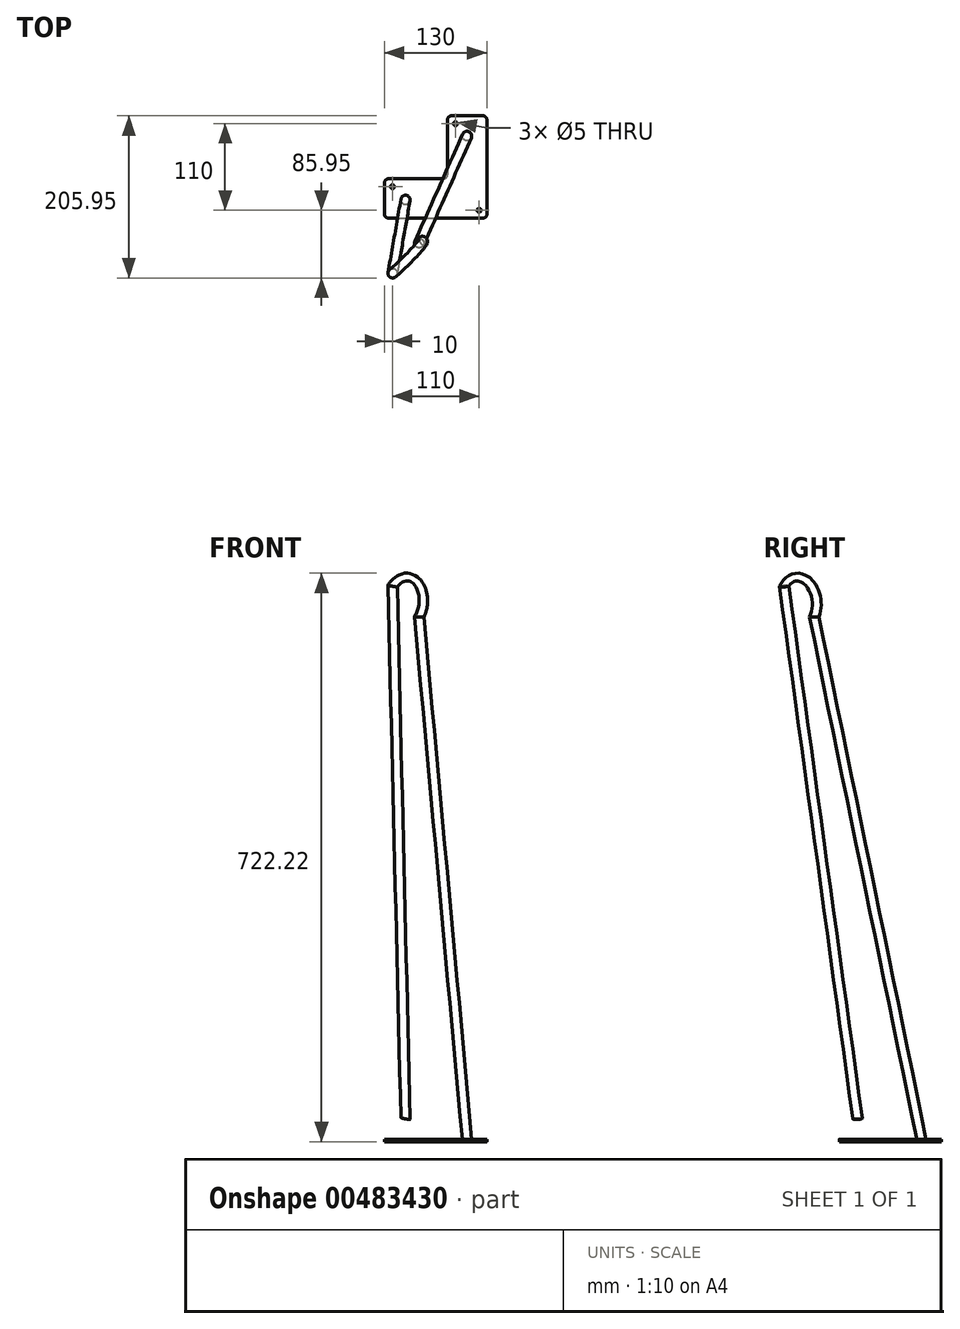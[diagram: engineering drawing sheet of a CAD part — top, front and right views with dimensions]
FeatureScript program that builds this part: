
annotation { "Feature Type Name" : "Feature", "Feature Type Description" : "" }
export const myFeature = defineFeature(function(context is Context, id is Id, definition is map)
    precondition{}
    {
        {
            var Q0;
            Q0=qCreatedBy(makeId("Top.planeOp"),FACE);
            var sketch = newSketch(context, id + "F0", { "sketchPlane" : qUnion([Q0])});
            skLineSegment(sketch, "E0", {"start": v(0, 0) * mm, "end": v(130, 0) * mm});
            skLineSegment(sketch, "E1", {"start": v(130, 0) * mm, "end": v(130, 130) * mm});
            skLineSegment(sketch, "E2", {"start": v(130, 130) * mm, "end": v(80, 130) * mm});
            skLineSegment(sketch, "E3", {"start": v(80, 130) * mm, "end": v(80, 50) * mm});
            skLineSegment(sketch, "E4", {"start": v(80, 50) * mm, "end": v(0, 50) * mm});
            skLineSegment(sketch, "E5", {"start": v(0, 50) * mm, "end": v(0, 0) * mm});
            skPoint(sketch, "E6", {"position": v(105, 105) * mm});
            skPoint(sketch, "E7", {"position": v(25, 25) * mm});
            skSolve(sketch);
        }
        {
            var Q0;
            Q0=makeQuery(id+"F0.imprint","IMPRINT",FACE,{"disambiguationData":[TD([[makeQuery(id+"F0.imprint","IMPRINT",EDGE,{"derivedFrom":sQuery(id+"F0.wireOp",EDGE,"E0")}),1.0]])]});
            extrude(context, id + "F1", {"entities" : qUnion([Q0]), "depth" : 3 * mm});
        }
        {
            var Q0;
            Q0=qCreatedBy(makeId("Top.planeOp"),FACE);
            cPlane(context, id + "F2", {"entities" : qUnion([Q0]), "cplaneType" : CPlaneType.OFFSET, "offset" : 704 * mm, "width" : 150 * mm, "height" : 150 * mm});
        }
        {
            var Q0;
            Q0=qCreatedBy(id+"F2.planeOp",FACE);
            var sketch = newSketch(context, id + "F3", { "sketchPlane" : qUnion([Q0])});
            skPoint(sketch, "E8", {"position": v(105, 25) * mm});
            skSolve(sketch);
        }
        {
            var Q0;
            Q0=sQuery(id+"F0.wireOp",VERTEX,"E7");
            var Q1;
            Q1=sQuery(id+"F0.wireOp",VERTEX,"E6");
            var Q2;
            Q2=sQuery(id+"F3.wireOp",VERTEX,"E8");
            cPlane(context, id + "F4", {"entities" : qUnion([Q0, Q1, Q2]), "cplaneType" : CPlaneType.THREE_POINT, "offset" : 25 * mm, "width" : 150 * mm, "height" : 150 * mm});
        }
        {
            var Q0;
            Q0=qCreatedBy(id+"F4.planeOp",FACE);
            var sketch = newSketch(context, id + "F5", { "sketchPlane" : qUnion([Q0])});
            skLineSegment(sketch, "E9", {"start": v(-148.02, 11.86) * mm, "end": v(-62.04, 689.58) * mm});
            skLineSegment(sketch, "E10", {"start": v(-12.25, 685.6) * mm, "end": v(-35.24, 2.82) * mm});
            skArc(sketch, "E11.filletArc", {"start": v(-12.25, 685.6) * mm, "mid": v(-35.24, 711.35) * mm, "end": v(-62.04, 689.58) * mm});
            skSolve(sketch);
        }
        {
            var Q0;
            Q0=qCreatedBy(makeId("Top.planeOp"),FACE);
            var sketch = newSketch(context, id + "F6", { "sketchPlane" : qUnion([Q0])});
            skCircle(sketch, "E12", {"center": v(105, 105) * mm, "radius": 6 * mm});
            skSolve(sketch);
        }
        {
            var Q0;
            Q0=qSketchRegion(id+"F6",true);
            var Q1;
            Q1=qConstructionFilter(qBodyType(qCreatedBy(id+"F5",EDGE),BodyType.WIRE),ConstructionObject.NO);
            sweep(context, id + "F7", {"operationType" : NewBodyOperationType.ADD, "profiles" : qUnion([Q0]), "path" : qUnion([Q1])});
        }
        {
            var Q0;
            Q0=qCreatedBy(makeId("Front.planeOp"),FACE);
            var sketch = newSketch(context, id + "F8", { "sketchPlane" : qUnion([Q0])});
            skLineSegment(sketch, "E13.bottom", {"start": v(0, 0) * mm, "end": v(130, 0) * mm});
            skLineSegment(sketch, "E13.top", {"start": v(0, -10) * mm, "end": v(130, -10) * mm});
            skLineSegment(sketch, "E13.left", {"start": v(0, 0) * mm, "end": v(0, -10) * mm});
            skLineSegment(sketch, "E13.right", {"start": v(130, 0) * mm, "end": v(130, -10) * mm});
            skSolve(sketch);
        }
        {
            var Q0;
            Q0=makeQuery(id+"F8.imprint","IMPRINT",FACE,{"disambiguationData":[TD([[makeQuery(id+"F8.imprint","IMPRINT",EDGE,{"derivedFrom":sQuery(id+"F8.wireOp",EDGE,"E13.bottom")}),-1.0]])]});
            extrude(context, id + "F9", {"entities" : qUnion([Q0]), "operationType" : NewBodyOperationType.REMOVE, "endBound" : BoundingType.THROUGH_ALL, "oppositeDirection" : true, "depth" : 25 * mm});
        }
        {
            var Q0;
            Q0=makeQuery(id+"F0.imprint","IMPRINT",FACE,{"disambiguationData":[TD([[makeQuery(id+"F0.imprint","IMPRINT",EDGE,{"derivedFrom":sQuery(id+"F0.wireOp",EDGE,"E0")}),1.0]])]});
            var sketch = newSketch(context, id + "F10", { "sketchPlane" : qUnion([Q0])});
            skPoint(sketch, "E14", {"position": v(90, 120) * mm});
            skPoint(sketch, "E15", {"position": v(120, 10) * mm});
            skPoint(sketch, "E16", {"position": v(10, 40) * mm});
            skSolve(sketch);
        }
        {
            var Q0;
            Q0=sQuery(id+"F10.wireOp",VERTEX,"E14");
            var Q1;
            Q1=sQuery(id+"F10.wireOp",VERTEX,"E15");
            var Q2;
            Q2=sQuery(id+"F10.wireOp",VERTEX,"E16");
            var Q3;
            Q3=makeQuery(id+"F1.opExtrude","SWEPT_BODY",BODY,{"disambiguationData":[OSD([sQuery(id+"F0.wireOp",EDGE,"E0"),sQuery(id+"F0.wireOp",EDGE,"E1"),sQuery(id+"F0.wireOp",EDGE,"E2"),sQuery(id+"F0.wireOp",EDGE,"E3"),sQuery(id+"F0.wireOp",EDGE,"E4"),sQuery(id+"F0.wireOp",EDGE,"E5")])]});
            hole(context, id + "F11", {"style" : HoleStyle.SIMPLE, "endStyle" : HoleEndStyle.BLIND, "oppositeDirection" : true, "standardTappedOrClearance" : lookupTablePath({ "standard" : "ISO", "size" : "5", "type" : "Drilled" }), "standardBlindInLast" : lookupTablePath({ "standard" : "ISO", "size" : "5", "type" : "Drilled" }), "holeDiameter" : 5 * mm, "holeDepth" : 30 * mm, "isTappedThrough" : true, "tappedDepth" : 12 * mm, "tapClearance" : 3, "locations" : qUnion([Q0, Q1, Q2]), "scope" : qUnion([Q3])});
        }
        {
            var Q0;
            Q0=makeQuery(id+"F1.opExtrude","SWEPT_EDGE",EDGE,{"disambiguationData":[OSD([sQuery(id+"F0.wireOp",EDGE,"E1"),sQuery(id+"F0.wireOp",EDGE,"E2")])]});
            var Q1;
            Q1=makeQuery(id+"F1.opExtrude","SWEPT_EDGE",EDGE,{"disambiguationData":[OSD([sQuery(id+"F0.wireOp",EDGE,"E2"),sQuery(id+"F0.wireOp",EDGE,"E3")])]});
            var Q2;
            Q2=makeQuery(id+"F1.opExtrude","SWEPT_EDGE",EDGE,{"disambiguationData":[OSD([sQuery(id+"F0.wireOp",EDGE,"E3"),sQuery(id+"F0.wireOp",EDGE,"E4")])]});
            var Q3;
            Q3=makeQuery(id+"F1.opExtrude","SWEPT_EDGE",EDGE,{"disambiguationData":[OSD([sQuery(id+"F0.wireOp",EDGE,"E4"),sQuery(id+"F0.wireOp",EDGE,"E5")])]});
            var Q4;
            Q4=makeQuery(id+"F1.opExtrude","SWEPT_EDGE",EDGE,{"disambiguationData":[OSD([sQuery(id+"F0.wireOp",EDGE,"E0"),sQuery(id+"F0.wireOp",EDGE,"E5")])]});
            var Q5;
            Q5=makeQuery(id+"F1.opExtrude","SWEPT_EDGE",EDGE,{"disambiguationData":[OSD([sQuery(id+"F0.wireOp",EDGE,"E0"),sQuery(id+"F0.wireOp",EDGE,"E1")])]});
            fillet(context, id + "F12", {"entities" : qUnion([Q0, Q1, Q2, Q3, Q4, Q5]), "radius" : 5 * mm, "tangentPropagation" : true, "allowEdgeOverflow" : false});
        }
    });
